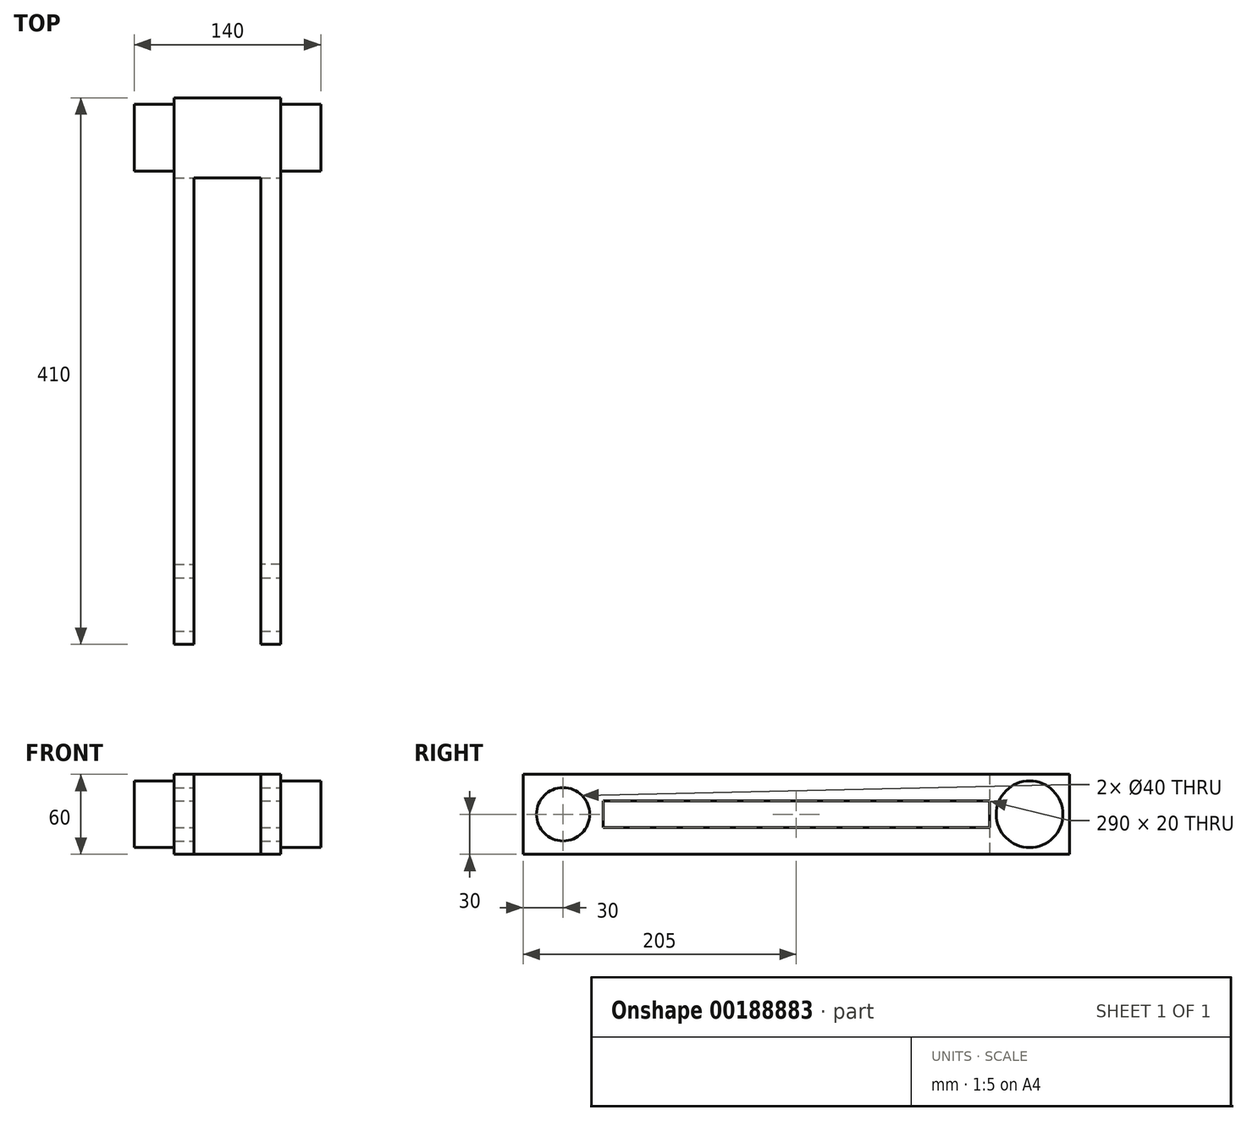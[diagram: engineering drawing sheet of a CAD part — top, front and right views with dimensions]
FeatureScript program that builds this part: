
annotation { "Feature Type Name" : "Feature", "Feature Type Description" : "" }
export const myFeature = defineFeature(function(context is Context, id is Id, definition is map)
    precondition{}
    {
        {
            var Q0;
            Q0=qCreatedBy(makeId("Right.planeOp"),FACE);
            var sketch = newSketch(context, id + "F0", { "sketchPlane" : qUnion([Q0])});
            skCircle(sketch, "E0", {"center": v(0, 0) * mm, "radius": 25 * mm});
            skSolve(sketch);
        }
        {
            var Q0;
            Q0=qSketchRegion(id+"F0",true);
            extrude(context, id + "F1", {"entities" : qUnion([Q0]), "depth" : 140 * mm});
        }
        {
            var Q0;
            Q0=qCreatedBy(makeId("Front.planeOp"),FACE);
            var sketch = newSketch(context, id + "F2", { "sketchPlane" : qUnion([Q0])});
            skLineSegment(sketch, "E1.bottom", {"start": v(30, 30) * mm, "end": v(110, 30) * mm});
            skLineSegment(sketch, "E1.top", {"start": v(30, -30) * mm, "end": v(110, -30) * mm});
            skLineSegment(sketch, "E1.left", {"start": v(30, 30) * mm, "end": v(30, -30) * mm});
            skLineSegment(sketch, "E1.right", {"start": v(110, 30) * mm, "end": v(110, -30) * mm});
            skSolve(sketch);
        }
        {
            var Q0;
            Q0=qSketchRegion(id+"F2",true);
            extrude(context, id + "F3", {"entities" : qUnion([Q0]), "operationType" : NewBodyOperationType.ADD, "depth" : 30 * mm, "hasSecondDirection" : true, "secondDirectionOppositeDirection" : true, "secondDirectionDepth" : 30 * mm});
        }
        {
            var Q0;
            Q0=makeQuery(id+"F3.opExtrude","CAP_FACE",FACE,{"disambiguationData":[OSD([sQuery(id+"F2.wireOp",EDGE,"E1.bottom"),sQuery(id+"F2.wireOp",EDGE,"E1.top"),sQuery(id+"F2.wireOp",EDGE,"E1.left"),sQuery(id+"F2.wireOp",EDGE,"E1.right")])],"isStart":false});
            var sketch = newSketch(context, id + "F4", { "sketchPlane" : qUnion([Q0])});
            skLineSegment(sketch, "E2.bottom", {"start": v(95, 30) * mm, "end": v(110, 30) * mm});
            skLineSegment(sketch, "E2.top", {"start": v(95, 10) * mm, "end": v(110, 10) * mm});
            skLineSegment(sketch, "E2.left", {"start": v(95, 30) * mm, "end": v(95, 10) * mm});
            skLineSegment(sketch, "E2.right", {"start": v(110, 30) * mm, "end": v(110, 10) * mm});
            skLineSegment(sketch, "E3.bottom", {"start": v(30, 30) * mm, "end": v(45, 30) * mm});
            skLineSegment(sketch, "E3.top", {"start": v(30, 10) * mm, "end": v(45, 10) * mm});
            skLineSegment(sketch, "E3.left", {"start": v(30, 30) * mm, "end": v(30, 10) * mm});
            skLineSegment(sketch, "E3.right", {"start": v(45, 30) * mm, "end": v(45, 10) * mm});
            skLineSegment(sketch, "E4.bottom", {"start": v(30, -10) * mm, "end": v(45, -10) * mm});
            skLineSegment(sketch, "E4.top", {"start": v(30, -30) * mm, "end": v(45, -30) * mm});
            skLineSegment(sketch, "E4.left", {"start": v(30, -10) * mm, "end": v(30, -30) * mm});
            skLineSegment(sketch, "E4.right", {"start": v(45, -10) * mm, "end": v(45, -30) * mm});
            skLineSegment(sketch, "E5.bottom", {"start": v(95, -10) * mm, "end": v(110, -10) * mm});
            skLineSegment(sketch, "E5.top", {"start": v(95, -30) * mm, "end": v(110, -30) * mm});
            skLineSegment(sketch, "E5.left", {"start": v(95, -10) * mm, "end": v(95, -30) * mm});
            skLineSegment(sketch, "E5.right", {"start": v(110, -10) * mm, "end": v(110, -30) * mm});
            skSolve(sketch);
        }
        {
            var Q0;
            Q0=qSketchRegion(id+"F4",true);
            extrude(context, id + "F5", {"entities" : qUnion([Q0]), "operationType" : NewBodyOperationType.ADD, "depth" : 350 * mm});
        }
        {
            var Q0;
            Q0=makeQuery(id+"F5.boolean.opBoolean","MERGE",FACE,{"derivedFrom":[makeQuery(id+"F3.opExtrude","SWEPT_FACE",FACE,{"disambiguationData":[OSD([sQuery(id+"F2.wireOp",EDGE,"E1.bottom")])]}),makeQuery(id+"F5.opExtrude","SWEPT_FACE",FACE,{"disambiguationData":[OSD([sQuery(id+"F4.wireOp",EDGE,"E2.bottom")])]}),makeQuery(id+"F5.opExtrude","SWEPT_FACE",FACE,{"disambiguationData":[OSD([sQuery(id+"F4.wireOp",EDGE,"E3.bottom")])]})]});
            var sketch = newSketch(context, id + "F6", { "sketchPlane" : qUnion([Q0])});
            skLineSegment(sketch, "E6.bottom", {"start": v(110, -380) * mm, "end": v(95, -380) * mm});
            skLineSegment(sketch, "E6.top", {"start": v(110, -320) * mm, "end": v(95, -320) * mm});
            skLineSegment(sketch, "E6.left", {"start": v(110, -380) * mm, "end": v(110, -320) * mm});
            skLineSegment(sketch, "E6.right", {"start": v(95, -380) * mm, "end": v(95, -320) * mm});
            skLineSegment(sketch, "E7.bottom", {"start": v(30, -380) * mm, "end": v(45, -380) * mm});
            skLineSegment(sketch, "E7.top", {"start": v(30, -320) * mm, "end": v(45, -320) * mm});
            skLineSegment(sketch, "E7.left", {"start": v(30, -380) * mm, "end": v(30, -320) * mm});
            skLineSegment(sketch, "E7.right", {"start": v(45, -380) * mm, "end": v(45, -320) * mm});
            skSolve(sketch);
        }
        {
            var Q0;
            Q0=qSketchRegion(id+"F6",true);
            extrude(context, id + "F7", {"entities" : qUnion([Q0]), "operationType" : NewBodyOperationType.ADD, "oppositeDirection" : true, "depth" : 50 * mm});
        }
        {
            var Q0;
            Q0=makeQuery(id+"F7.boolean.opBoolean","MERGE",FACE,{"derivedFrom":[makeQuery(id+"F5.boolean.opBoolean","MERGE",FACE,{"derivedFrom":[makeQuery(id+"F3.opExtrude","SWEPT_FACE",FACE,{"disambiguationData":[OSD([sQuery(id+"F2.wireOp",EDGE,"E1.right")])]}),makeQuery(id+"F5.opExtrude","SWEPT_FACE",FACE,{"disambiguationData":[OSD([sQuery(id+"F4.wireOp",EDGE,"E2.right")])]}),makeQuery(id+"F5.opExtrude","SWEPT_FACE",FACE,{"disambiguationData":[OSD([sQuery(id+"F4.wireOp",EDGE,"E5.right")])]})]}),makeQuery(id+"F7.opExtrude","SWEPT_FACE",FACE,{"disambiguationData":[OSD([sQuery(id+"F6.wireOp",EDGE,"E6.left")])]})]});
            var sketch = newSketch(context, id + "F8", { "sketchPlane" : qUnion([Q0])});
            skCircle(sketch, "E8", {"center": v(-350, 0) * mm, "radius": 20 * mm});
            skSolve(sketch);
        }
        {
            var Q0;
            Q0=qSketchRegion(id+"F8",true);
            extrude(context, id + "F9", {"entities" : qUnion([Q0]), "operationType" : NewBodyOperationType.REMOVE, "endBound" : BoundingType.THROUGH_ALL, "oppositeDirection" : true, "depth" : 25 * mm});
        }
    });
